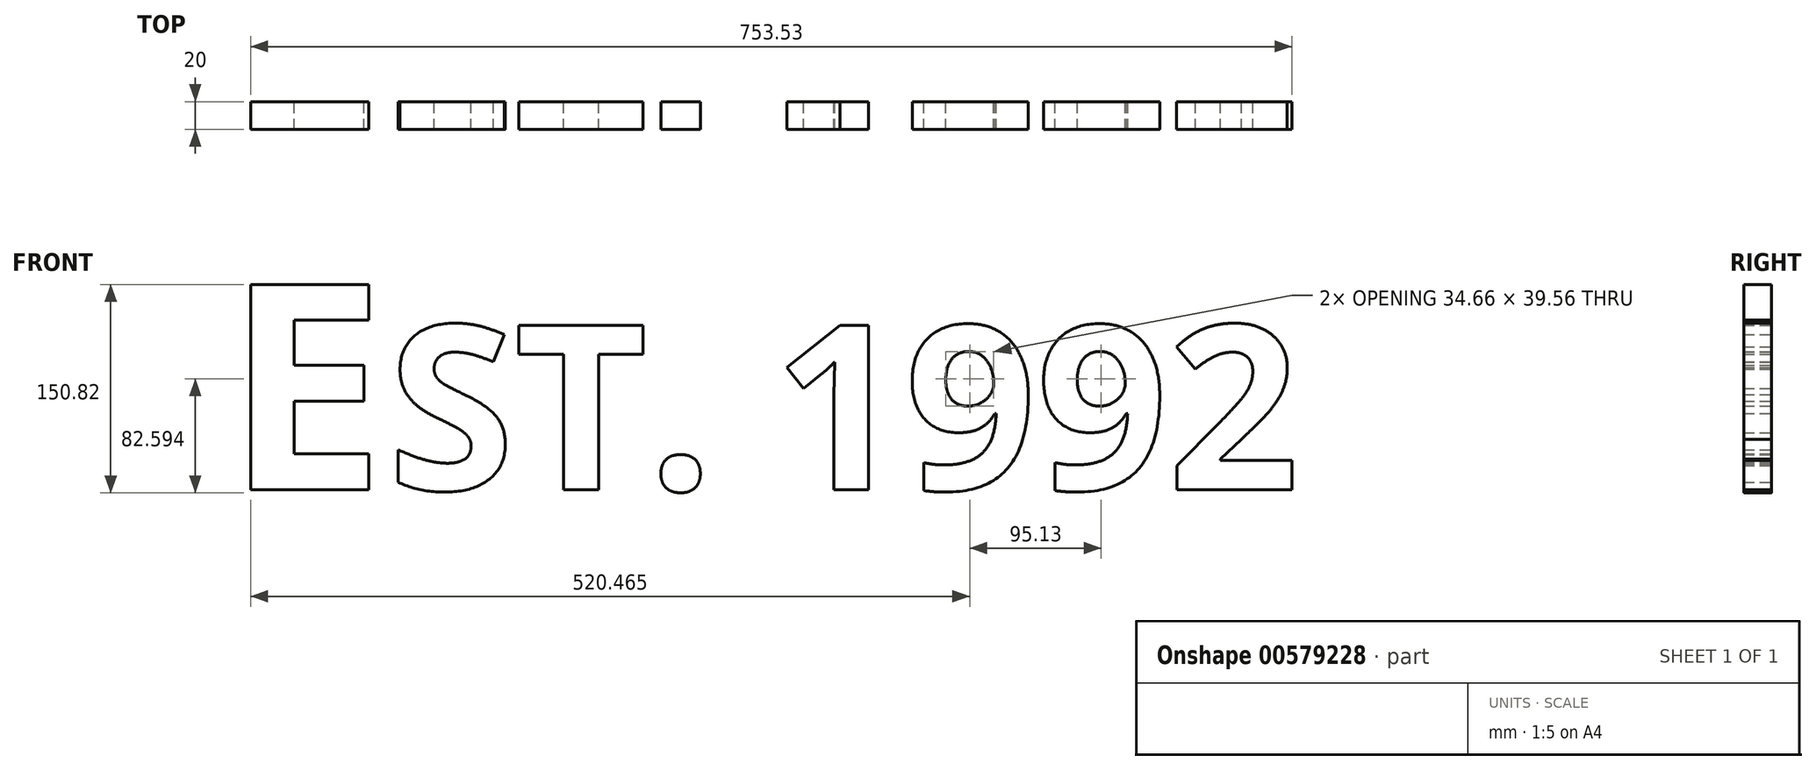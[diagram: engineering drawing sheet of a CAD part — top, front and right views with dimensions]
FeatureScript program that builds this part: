
annotation { "Feature Type Name" : "Feature", "Feature Type Description" : "" }
export const myFeature = defineFeature(function(context is Context, id is Id, definition is map)
    precondition{}
    {
        {
            var Q0;
            Q0=qCreatedBy(makeId("Front.planeOp"),FACE);
            var sketch = newSketch(context, id + "F0", { "sketchPlane" : qUnion([Q0])});
            skText(sketch, "E0", { "text": "E", "fontName": "OpenSans-Bold.ttf"});
            skText(sketch, "E1", { "text": "ST. 1992", "fontName": "OpenSans-Bold.ttf"});
            const initialGuessF0  = {"E0": [-0.5046, -0.07508, 1, 0, 0.15], "E1": [-0.38673, -0.07498, 1, 0, 0.12]};
            skSetInitialGuess(sketch, initialGuessF0);
            skSolve(sketch);
        }
        {
            var Q0;
            Q0 = qSketchRegion(id + "F0", true);
            extrude(context, id + "F1", {"entities" : qUnion([Q0]), "depth" : 20 * mm, "offsetDistance" : 25 * mm});
        }
    });
